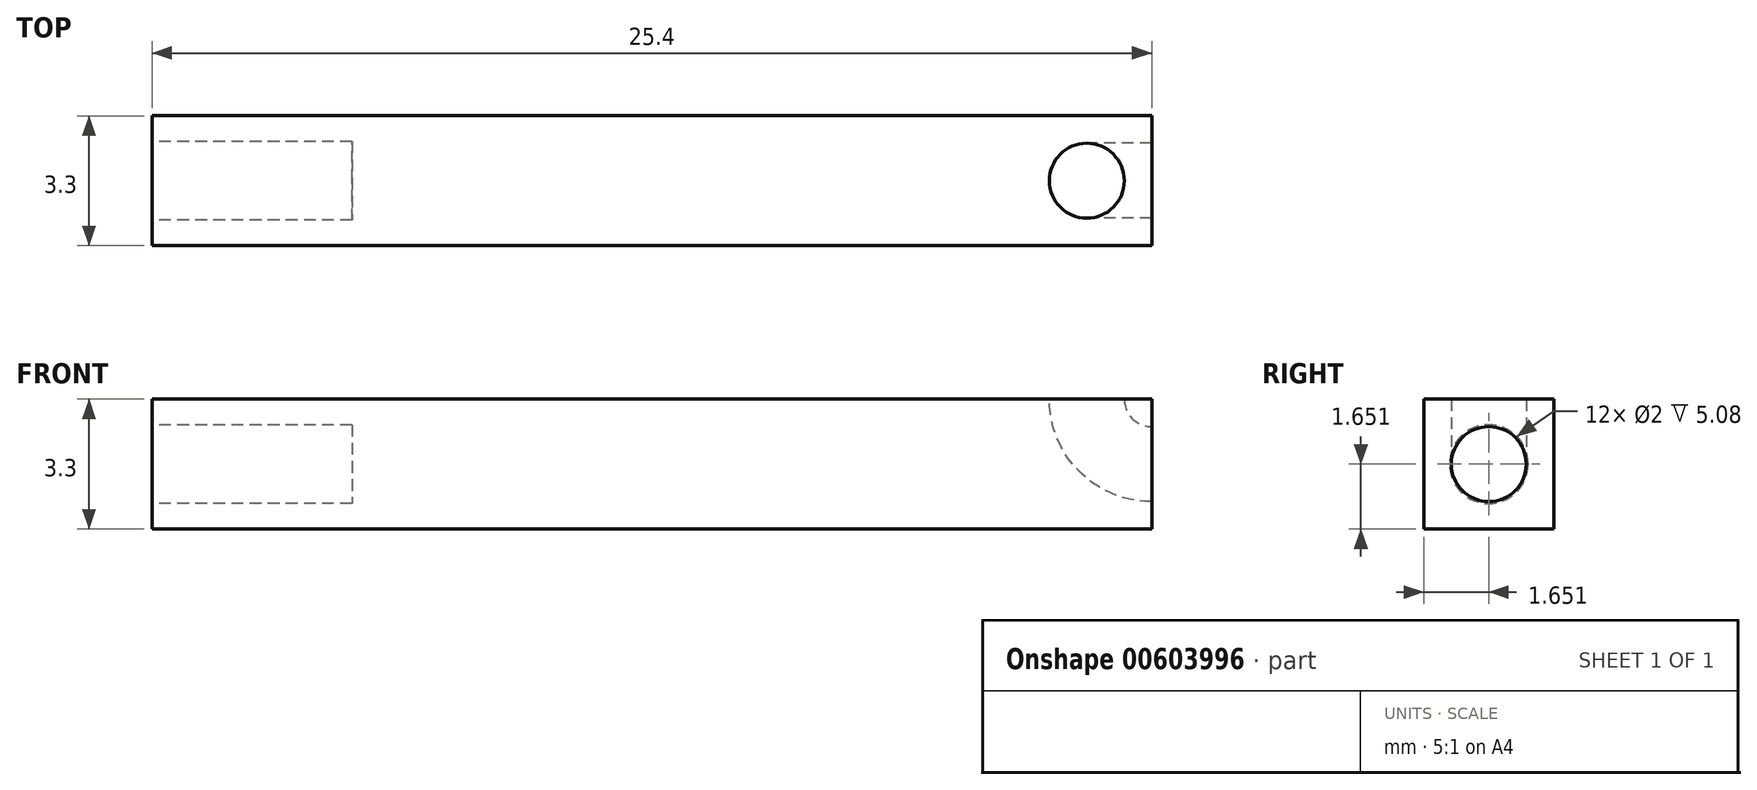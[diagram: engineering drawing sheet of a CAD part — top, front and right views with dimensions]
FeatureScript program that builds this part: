
annotation { "Feature Type Name" : "Feature", "Feature Type Description" : "" }
export const myFeature = defineFeature(function(context is Context, id is Id, definition is map)
    precondition{}
    {
        {
            var Q0;
            Q0=qCreatedBy(makeId("Top.planeOp"),FACE);
            var sketch = newSketch(context, id + "F0", { "sketchPlane" : qUnion([Q0])});
            skLineSegment(sketch, "E0.bottom", {"start": v(0, 0) * mm, "end": v(25.4, 0) * mm});
            skLineSegment(sketch, "E0.top", {"start": v(0, 3.3) * mm, "end": v(25.4, 3.3) * mm});
            skLineSegment(sketch, "E0.left", {"start": v(0, 0) * mm, "end": v(0, 3.3) * mm});
            skLineSegment(sketch, "E0.right", {"start": v(25.4, 0) * mm, "end": v(25.4, 3.3) * mm});
            skSolve(sketch);
        }
        {
            var Q0;
            Q0 = qSketchRegion(id + "F0", true);
            extrude(context, id + "F1", {"entities" : qUnion([Q0]), "depth" : 3.3 * mm, "offsetDistance" : 25.4 * mm});
        }
        {
            var Q0;
            Q0=makeQuery(id+"F1.opExtrude","SWEPT_FACE",FACE,{"disambiguationData":[OSD([sQuery(id+"F0.wireOp",EDGE,"E0.left")])]});
            var sketch = newSketch(context, id + "F2", { "sketchPlane" : qUnion([Q0])});
            skCircle(sketch, "E1", {"center": v(-1.65, 1.65) * mm, "radius": 1 * mm});
            skSolve(sketch);
        }
        {
            var Q0;
            Q0=makeQuery(id+"F2.imprint","IMPRINT",FACE,{"disambiguationData":[TD([[makeQuery(id+"F2.imprint","IMPRINT",EDGE,{"derivedFrom":sQuery(id+"F2.wireOp",EDGE,"E1")}),1.0]])]});
            extrude(context, id + "F3", {"entities" : qUnion([Q0]), "operationType" : NewBodyOperationType.REMOVE, "oppositeDirection" : true, "depth" : 5.08 * mm, "offsetDistance" : 25.4 * mm});
        }
        {
            var Q0;
            Q0=makeQuery(id+"F1.opExtrude","SWEPT_FACE",FACE,{"disambiguationData":[OSD([sQuery(id+"F0.wireOp",EDGE,"E0.right")])]});
            var sketch = newSketch(context, id + "F4", { "sketchPlane" : qUnion([Q0])});
            skCircle(sketch, "E2", {"center": v(1.65, 1.65) * mm, "radius": 0.95 * mm});
            skSolve(sketch);
        }
        {
            var Q0;
            Q0=makeQuery(id+"F1.opExtrude","SWEPT_FACE",FACE,{"disambiguationData":[OSD([sQuery(id+"F0.wireOp",EDGE,"E0.bottom")])]});
            cPlane(context, id + "F5", {"entities" : qUnion([Q0]), "cplaneType" : CPlaneType.OFFSET, "offset" : 1.65 * mm, "oppositeDirection" : true, "width" : 152.4 * mm, "height" : 152.4 * mm});
        }
        {
            var Q0;
            Q0=qCreatedBy(id+"F5.planeOp",FACE);
            var sketch = newSketch(context, id + "F6", { "sketchPlane" : qUnion([Q0])});
            skArc(sketch, "E3", {"start": v(23.75, 3.3) * mm, "mid": v(24.23, 2.13) * mm, "end": v(25.4, 1.65) * mm});
            skSolve(sketch);
        }
        {
            var Q0;
            Q0=makeQuery(id+"F4.imprint","IMPRINT",FACE,{"disambiguationData":[TD([[makeQuery(id+"F4.imprint","IMPRINT",EDGE,{"derivedFrom":sQuery(id+"F4.wireOp",EDGE,"E2")}),1.0]])]});
            var Q1;
            Q1=sQuery(id+"F4.wireOp",EDGE,"E2");
            var Q2;
            Q2=sQuery(id+"F6.wireOp",EDGE,"E3");
            sweep(context, id + "F7", {"operationType" : NewBodyOperationType.REMOVE, "profiles" : qUnion([Q0]), "surfaceProfiles" : qUnion([Q1]), "path" : qUnion([Q2])});
        }
    });
